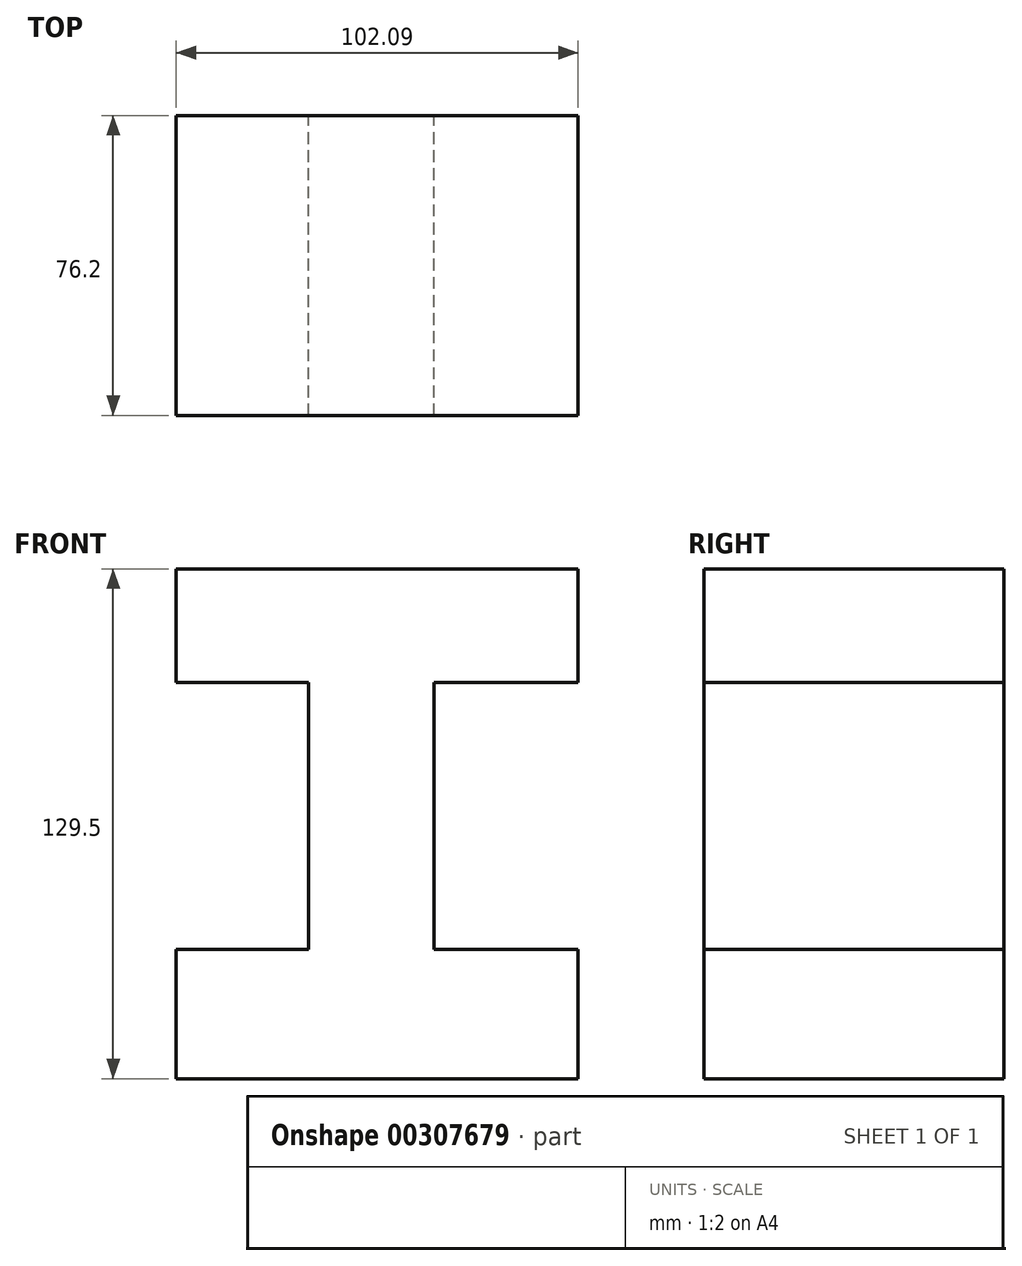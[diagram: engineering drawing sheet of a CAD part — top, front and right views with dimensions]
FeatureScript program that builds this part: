
annotation { "Feature Type Name" : "Feature", "Feature Type Description" : "" }
export const myFeature = defineFeature(function(context is Context, id is Id, definition is map)
    precondition{}
    {
        {
            var Q0;
            Q0=qCreatedBy(makeId("Front.planeOp"),FACE);
            var sketch = newSketch(context, id + "F0", { "sketchPlane" : qUnion([Q0])});
            skLineSegment(sketch, "E0", {"start": v(-53.44, -55.33) * mm, "end": v(48.65, -55.33) * mm});
            skLineSegment(sketch, "E1", {"start": v(48.65, -55.33) * mm, "end": v(48.65, -22.44) * mm});
            skLineSegment(sketch, "E2", {"start": v(48.65, -22.44) * mm, "end": v(12, -22.44) * mm});
            skLineSegment(sketch, "E3", {"start": v(12, -22.44) * mm, "end": v(12, 45.4) * mm});
            skLineSegment(sketch, "E4", {"start": v(12, 45.4) * mm, "end": v(48.65, 45.4) * mm});
            skLineSegment(sketch, "E5", {"start": v(48.65, 45.4) * mm, "end": v(48.65, 74.17) * mm});
            skLineSegment(sketch, "E6", {"start": v(48.65, 74.17) * mm, "end": v(-53.44, 74.17) * mm});
            skLineSegment(sketch, "E7", {"start": v(-53.44, 74.17) * mm, "end": v(-53.44, 45.4) * mm});
            skLineSegment(sketch, "E8", {"start": v(-53.44, 45.4) * mm, "end": v(-19.87, 45.4) * mm});
            skLineSegment(sketch, "E9", {"start": v(-19.87, 45.4) * mm, "end": v(-19.87, -22.44) * mm});
            skLineSegment(sketch, "E10", {"start": v(-19.87, -22.44) * mm, "end": v(-53.44, -22.44) * mm});
            skLineSegment(sketch, "E11", {"start": v(-53.44, -22.44) * mm, "end": v(-53.44, -55.33) * mm});
            skSolve(sketch);
        }
        {
            var Q0;
            Q0=makeQuery(id+"F0.imprint","IMPRINT",FACE,{"disambiguationData":[TD([[makeQuery(id+"F0.imprint","IMPRINT",EDGE,{"derivedFrom":sQuery(id+"F0.wireOp",EDGE,"E0")}),1.0]])]});
            extrude(context, id + "F1", {"entities" : qUnion([Q0]), "depth" : 76.2 * mm});
        }
    });
